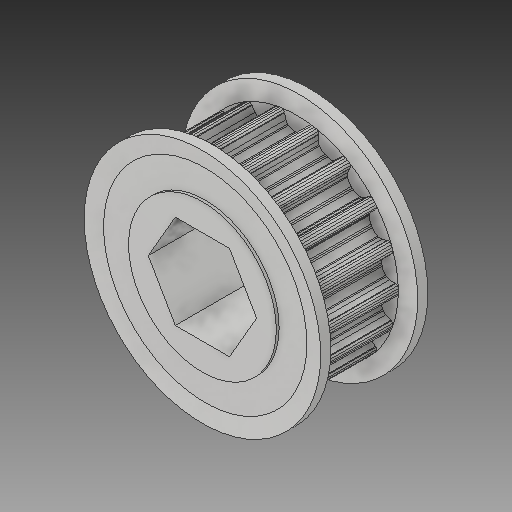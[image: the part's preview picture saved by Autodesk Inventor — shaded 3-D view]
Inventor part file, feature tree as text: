
AUTODESK INVENTOR PART (.ipt)
format: ipt  version: 2017 (Build 210142000, 142)  size: 547,328 bytes
history: native  units: in
note: dims shown in document units (in); Inventor stores cm internally (conversion verified against a paired STEP export)
features: mirror x1
ambient origin geometry x8: Origin, YZ Plane, XZ Plane, XY Plane, X Axis, Y Axis, Z Axis, Center Point
bodies: Solid1 (feature_tree)
feature tree (1):
  mirror  "Mirror1"
